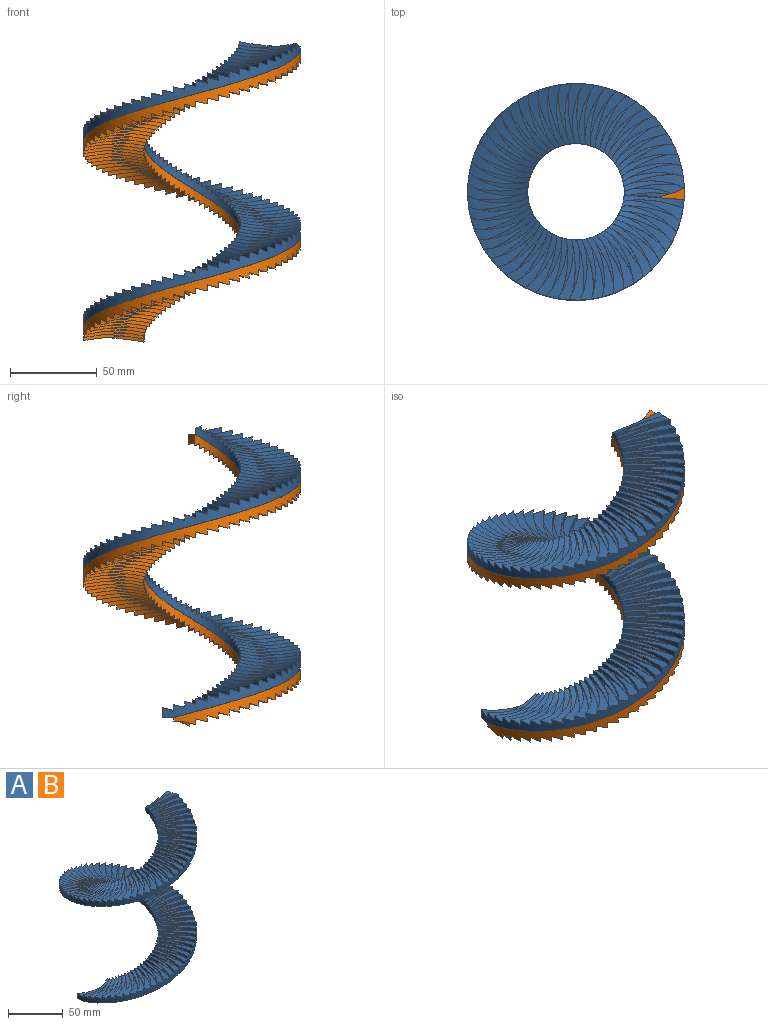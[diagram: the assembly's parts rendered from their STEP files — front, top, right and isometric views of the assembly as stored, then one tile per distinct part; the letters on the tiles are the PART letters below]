
ASSEMBLY  parts=2 mates=1
PART A: 370 faces, bbox 134.9x134.9x181.6 mm
  f0: plane 2.58x1.01mm, normal (0,0,-1), area 1mm2, adj f2,f184,f369
  f1: bspline ~40.21x16.63mm, area 94.5mm2, adj f2,f3,f4,f185,f368
  f2: cylinder r=27.93mm len=168.65mm, axis (0,0,-1), area 1520.9mm2, adj f0,f1,f4,f5,f6,f7,f8,f9
  f3: cylinder r=62.62mm len=167.8mm, axis (0,0,-1), area 3554.3mm2, adj f1,f185,f186,f187,f188,f189,f190,f191
  f4: bspline ~39.85x15.98mm, area 49.6mm2, adj f1,f2,f5,f185
  f5: bspline ~38.72x13.77mm, area 65.8mm2, adj f2,f4,f6,f185,f186
  f6: bspline ~37.98x15.95mm, area 41.2mm2, adj f2,f5,f7,f186,f187,f188
  f7: bspline ~39.79x14.14mm, area 55mm2, adj f2,f6,f8,f188
  f8: bspline ~37.93x15.94mm, area 41.3mm2, adj f2,f7,f9,f188,f189,f190
  f9: bspline ~40.42x16.75mm, area 66.7mm2, adj f2,f8,f10,f190
  f10: bspline ~37.46x15.96mm, area 41.2mm2, adj f2,f9,f11,f190,f191,f192
  f11: bspline ~40.61x19.84mm, area 66.8mm2, adj f2,f10,f12,f192
  f12: bspline ~36.57x15.97mm, area 41.2mm2, adj f2,f11,f13,f192,f193,f194
  f13: bspline ~40.36x23.15mm, area 54.7mm2, adj f2,f12,f14,f194
  f14: bspline ~35.31x15.95mm, area 41.2mm2, adj f2,f13,f15,f194,f195,f196
  f15: bspline ~39.67x26.21mm, area 66.4mm2, adj f2,f14,f16,f196
  f16: bspline ~33.65x17.74mm, area 41.3mm2, adj f2,f15,f17,f196,f197,f198
  f17: bspline ~38.53x28.98mm, area 66.8mm2, adj f2,f16,f18,f198
  f18: bspline ~31.59x21.16mm, area 41.2mm2, adj f2,f17,f19,f198,f199,f200
  f19: bspline ~36.98x31.43mm, area 66.5mm2, adj f2,f18,f20,f200
  f20: bspline ~29.21x24.34mm, area 41.2mm2, adj f2,f19,f21,f200,f201,f202
  f21: bspline ~35.03x33.54mm, area 54.8mm2, adj f2,f20,f22,f202
  f22: bspline ~27.26x26.55mm, area 41.2mm2, adj f2,f21,f23,f202,f203,f204
  f23: bspline ~35.28x32.68mm, area 66.5mm2, adj f2,f22,f24,f204
  f24: bspline ~29.88x23.55mm, area 41.3mm2, adj f2,f23,f25,f204,f205,f206
  f25: bspline ~36.63x29.97mm, area 66.9mm2, adj f2,f24,f26,f206
  f26: bspline ~32.17x20.27mm, area 41.2mm2, adj f2,f25,f27,f206,f207,f208
  f27: bspline ~37.58x26.95mm, area 54.9mm2, adj f2,f26,f28,f208
  f28: bspline ~34.11x16.81mm, area 41.2mm2, adj f2,f27,f29,f208,f209,f210
  f29: bspline ~38.12x23.63mm, area 54.9mm2, adj f2,f28,f30,f210
  f30: bspline ~35.67x15.94mm, area 41.3mm2, adj f2,f29,f31,f210,f211,f212
  f31: bspline ~38.25x20.05mm, area 66.6mm2, adj f2,f30,f32,f212
  f32: bspline ~36.84x15.95mm, area 41.3mm2, adj f2,f31,f33,f212,f213,f214
  f33: bspline ~37.95x16.63mm, area 67.1mm2, adj f2,f32,f34,f214
  f34: bspline ~37.61x15.98mm, area 41.2mm2, adj f2,f33,f35,f214,f215
  f35: bspline ~38.72x13.77mm, area 65.8mm2, adj f2,f34,f36,f215,f216
  f36: bspline ~37.98x15.95mm, area 41.2mm2, adj f2,f35,f37,f216,f217,f218
  f37: bspline ~39.79x14.14mm, area 55mm2, adj f2,f36,f38,f218
  f38: bspline ~37.93x15.94mm, area 41.3mm2, adj f2,f37,f39,f218,f219,f220
  f39: bspline ~40.42x16.75mm, area 66.7mm2, adj f2,f38,f40,f220
  f40: bspline ~37.46x15.96mm, area 41.2mm2, adj f2,f39,f41,f220,f221,f222
  f41: bspline ~40.61x19.84mm, area 66.8mm2, adj f2,f40,f42,f222
  f42: bspline ~36.57x15.97mm, area 41.2mm2, adj f2,f41,f43,f222,f223,f224
  f43: bspline ~40.36x23.15mm, area 54.7mm2, adj f2,f42,f44,f224
  f44: bspline ~35.31x15.95mm, area 41.2mm2, adj f2,f43,f45,f224,f225,f226
  f45: bspline ~39.67x26.21mm, area 66.4mm2, adj f2,f44,f46,f226
  f46: bspline ~33.65x17.74mm, area 41.3mm2, adj f2,f45,f47,f226,f227,f228
  f47: bspline ~38.53x28.98mm, area 66.8mm2, adj f2,f46,f48,f228
  f48: bspline ~31.59x21.16mm, area 41.2mm2, adj f2,f47,f49,f228,f229,f230
  f49: bspline ~36.98x31.43mm, area 66.5mm2, adj f2,f48,f50,f230
  f50: bspline ~29.21x24.35mm, area 41.2mm2, adj f2,f49,f51,f230,f231,f232
  f51: bspline ~35.03x33.54mm, area 54.8mm2, adj f2,f50,f52,f232
  f52: bspline ~27.26x26.55mm, area 41.2mm2, adj f2,f51,f53,f232,f233,f234
  f53: bspline ~35.28x32.68mm, area 66.5mm2, adj f2,f52,f54,f234
  f54: bspline ~29.88x23.55mm, area 41.3mm2, adj f2,f53,f55,f234,f235,f236
  f55: bspline ~36.63x29.97mm, area 66.9mm2, adj f2,f54,f56,f236
  f56: bspline ~32.17x20.27mm, area 41.2mm2, adj f2,f55,f57,f236,f237,f238
  f57: bspline ~37.58x26.95mm, area 54.9mm2, adj f2,f56,f58,f238
  f58: bspline ~34.11x16.81mm, area 41.2mm2, adj f2,f57,f59,f238,f239,f240
  f59: bspline ~38.12x23.63mm, area 54.9mm2, adj f2,f58,f60,f240
  f60: bspline ~35.67x15.94mm, area 41.3mm2, adj f2,f59,f61,f240,f241,f242
  f61: bspline ~38.25x20.05mm, area 66.6mm2, adj f2,f60,f62,f242
  f62: bspline ~36.84x15.95mm, area 41.3mm2, adj f2,f61,f63,f242,f243,f244
  f63: bspline ~37.95x16.63mm, area 67.1mm2, adj f2,f62,f64,f244
  f64: bspline ~37.61x15.98mm, area 41.2mm2, adj f2,f63,f65,f244,f245
  f65: bspline ~38.72x13.77mm, area 65.8mm2, adj f2,f64,f66,f245,f246
  f66: bspline ~37.98x15.95mm, area 41.2mm2, adj f2,f65,f67,f246,f247,f248
  f67: bspline ~39.79x14.14mm, area 55mm2, adj f2,f66,f68,f248
  f68: bspline ~37.93x15.94mm, area 41.3mm2, adj f2,f67,f69,f248,f249,f250
  f69: bspline ~40.42x16.75mm, area 66.7mm2, adj f2,f68,f70,f250
  f70: bspline ~37.46x15.96mm, area 41.2mm2, adj f2,f69,f71,f250,f251,f252
  f71: bspline ~40.61x19.84mm, area 66.8mm2, adj f2,f70,f72,f252
  f72: bspline ~36.57x15.97mm, area 41.2mm2, adj f2,f71,f73,f252,f253,f254
  f73: bspline ~40.36x23.15mm, area 54.7mm2, adj f2,f72,f74,f254
  f74: bspline ~35.31x15.95mm, area 41.2mm2, adj f2,f73,f75,f254,f255,f256
  f75: bspline ~39.67x26.21mm, area 66.4mm2, adj f2,f74,f76,f256
  f76: bspline ~33.65x17.74mm, area 41.3mm2, adj f2,f75,f77,f256,f257,f258
  f77: bspline ~38.53x28.98mm, area 66.8mm2, adj f2,f76,f78,f258
  f78: bspline ~31.59x21.16mm, area 41.2mm2, adj f2,f77,f79,f258,f259,f260
  f79: bspline ~36.98x31.43mm, area 66.5mm2, adj f2,f78,f80,f260
  f80: bspline ~29.21x24.34mm, area 41.2mm2, adj f2,f79,f81,f260,f261,f262
  f81: bspline ~35.03x33.54mm, area 54.8mm2, adj f2,f80,f82,f262
  f82: bspline ~27.26x26.55mm, area 41.2mm2, adj f2,f81,f83,f262,f263,f264
  f83: bspline ~35.28x32.68mm, area 66.5mm2, adj f2,f82,f84,f264
  f84: bspline ~29.88x23.55mm, area 41.3mm2, adj f2,f83,f85,f264,f265,f266
  f85: bspline ~36.63x29.97mm, area 66.9mm2, adj f2,f84,f86,f266
  f86: bspline ~32.17x20.27mm, area 41.2mm2, adj f2,f85,f87,f266,f267,f268
  f87: bspline ~37.58x26.95mm, area 54.9mm2, adj f2,f86,f88,f268
  f88: bspline ~34.11x16.81mm, area 41.2mm2, adj f2,f87,f89,f268,f269,f270
  f89: bspline ~38.12x23.63mm, area 54.9mm2, adj f2,f88,f90,f270
  f90: bspline ~35.67x15.94mm, area 41.3mm2, adj f2,f89,f91,f270,f271,f272
  f91: bspline ~38.25x20.05mm, area 66.6mm2, adj f2,f90,f92,f272
  f92: bspline ~36.84x15.95mm, area 41.3mm2, adj f2,f91,f93,f272,f273,f274
  f93: bspline ~37.95x16.63mm, area 67.1mm2, adj f2,f92,f94,f274
  f94: bspline ~37.61x15.98mm, area 41.2mm2, adj f2,f93,f95,f274,f275
  f95: bspline ~38.72x13.77mm, area 65.8mm2, adj f2,f94,f96,f275,f276
  f96: bspline ~37.98x15.95mm, area 41.2mm2, adj f2,f95,f97,f276,f277,f278
  f97: bspline ~39.79x14.14mm, area 55mm2, adj f2,f96,f98,f278
  f98: bspline ~37.93x15.94mm, area 41.3mm2, adj f2,f97,f99,f278,f279,f280
  f99: bspline ~40.42x16.75mm, area 66.7mm2, adj f2,f98,f100,f280
  f100: bspline ~37.46x15.96mm, area 41.2mm2, adj f2,f99,f101,f280,f281,f282
  f101: bspline ~40.61x19.84mm, area 66.8mm2, adj f2,f100,f102,f282
  f102: bspline ~36.57x15.97mm, area 41.2mm2, adj f2,f101,f103,f282,f283,f284
  f103: bspline ~40.36x23.15mm, area 54.7mm2, adj f2,f102,f104,f284
  f104: bspline ~35.31x15.95mm, area 41.2mm2, adj f2,f103,f105,f284,f285,f286
  f105: bspline ~39.67x26.21mm, area 66.4mm2, adj f2,f104,f106,f286
  f106: bspline ~33.65x17.74mm, area 41.3mm2, adj f2,f105,f107,f286,f287,f288
  f107: bspline ~38.53x28.98mm, area 66.8mm2, adj f2,f106,f108,f288
  f108: bspline ~31.59x21.16mm, area 41.2mm2, adj f2,f107,f109,f288,f289,f290
  f109: bspline ~36.98x31.43mm, area 66.5mm2, adj f2,f108,f110,f290
  f110: bspline ~29.21x24.35mm, area 41.2mm2, adj f2,f109,f111,f290,f291,f292
  f111: bspline ~35.03x33.54mm, area 54.8mm2, adj f2,f110,f112,f292
  f112: bspline ~27.26x26.55mm, area 41.2mm2, adj f2,f111,f113,f292,f293,f294
  f113: bspline ~35.28x32.68mm, area 66.5mm2, adj f2,f112,f114,f294
  f114: bspline ~29.88x23.55mm, area 41.3mm2, adj f2,f113,f115,f294,f295,f296
  f115: bspline ~36.63x29.97mm, area 66.9mm2, adj f2,f114,f116,f296
  f116: bspline ~32.17x20.27mm, area 41.2mm2, adj f2,f115,f117,f296,f297,f298
  f117: bspline ~37.58x26.95mm, area 54.9mm2, adj f2,f116,f118,f298
  f118: bspline ~34.11x16.81mm, area 41.2mm2, adj f2,f117,f119,f298,f299,f300
  f119: bspline ~38.12x23.63mm, area 54.9mm2, adj f2,f118,f120,f300
  f120: bspline ~35.67x15.94mm, area 41.3mm2, adj f2,f119,f121,f300,f301,f302
  f121: bspline ~38.25x20.05mm, area 66.6mm2, adj f2,f120,f122,f302
  f122: bspline ~36.84x15.95mm, area 41.3mm2, adj f2,f121,f123,f302,f303,f304
  f123: bspline ~37.95x16.63mm, area 67.1mm2, adj f2,f122,f124,f304
  f124: bspline ~37.61x15.98mm, area 41.2mm2, adj f2,f123,f125,f304,f305
  f125: bspline ~38.72x13.77mm, area 65.8mm2, adj f2,f124,f126,f305,f306
  f126: bspline ~37.98x15.95mm, area 41.2mm2, adj f2,f125,f127,f306,f307,f308
  f127: bspline ~39.79x14.14mm, area 55mm2, adj f2,f126,f128,f308
  f128: bspline ~37.93x15.94mm, area 41.3mm2, adj f2,f127,f129,f308,f309,f310
  f129: bspline ~40.42x16.75mm, area 66.7mm2, adj f2,f128,f130,f310
  f130: bspline ~37.46x15.96mm, area 41.2mm2, adj f2,f129,f131,f310,f311,f312
  f131: bspline ~40.61x19.84mm, area 66.8mm2, adj f2,f130,f132,f312
  f132: bspline ~36.57x15.97mm, area 41.2mm2, adj f2,f131,f133,f312,f313,f314
  f133: bspline ~40.36x23.15mm, area 54.7mm2, adj f2,f132,f134,f314
  f134: bspline ~35.31x15.95mm, area 41.2mm2, adj f2,f133,f135,f314,f315,f316
  f135: bspline ~39.67x26.21mm, area 66.4mm2, adj f2,f134,f136,f316
  f136: bspline ~33.65x17.74mm, area 41.3mm2, adj f2,f135,f137,f316,f317,f318
  f137: bspline ~38.53x28.98mm, area 66.8mm2, adj f2,f136,f138,f318
  f138: bspline ~31.59x21.16mm, area 41.2mm2, adj f2,f137,f139,f318,f319,f320
  f139: bspline ~36.98x31.43mm, area 66.5mm2, adj f2,f138,f140,f320
  f140: bspline ~29.21x24.34mm, area 41.2mm2, adj f2,f139,f141,f320,f321,f322
  f141: bspline ~35.03x33.54mm, area 54.8mm2, adj f2,f140,f142,f322
  f142: bspline ~27.26x26.55mm, area 41.2mm2, adj f2,f141,f143,f322,f323,f324
  f143: bspline ~35.28x32.68mm, area 66.5mm2, adj f2,f142,f144,f324
  f144: bspline ~29.88x23.55mm, area 41.3mm2, adj f2,f143,f145,f324,f325,f326
  f145: bspline ~36.63x29.97mm, area 66.9mm2, adj f2,f144,f146,f326
  f146: bspline ~32.17x20.27mm, area 41.2mm2, adj f2,f145,f147,f326,f327,f328
  f147: bspline ~37.58x26.95mm, area 54.9mm2, adj f2,f146,f148,f328
  f148: bspline ~34.11x16.81mm, area 41.2mm2, adj f2,f147,f149,f328,f329,f330
  f149: bspline ~38.12x23.63mm, area 54.9mm2, adj f2,f148,f150,f330
  f150: bspline ~35.67x15.94mm, area 41.3mm2, adj f2,f149,f151,f330,f331,f332
  f151: bspline ~38.25x20.05mm, area 66.6mm2, adj f2,f150,f152,f332
  f152: bspline ~36.84x15.95mm, area 41.3mm2, adj f2,f151,f153,f332,f333,f334
  f153: bspline ~37.95x16.63mm, area 67.1mm2, adj f2,f152,f154,f334
  f154: bspline ~37.61x15.98mm, area 41.2mm2, adj f2,f153,f155,f334,f335
  f155: bspline ~38.72x13.77mm, area 65.8mm2, adj f2,f154,f156,f335,f336
  f156: bspline ~37.98x15.95mm, area 41.2mm2, adj f2,f155,f157,f336,f337,f338
  f157: bspline ~39.79x14.14mm, area 55mm2, adj f2,f156,f158,f338
  f158: bspline ~37.93x15.94mm, area 41.3mm2, adj f2,f157,f159,f338,f339,f340
  f159: bspline ~40.42x16.75mm, area 66.7mm2, adj f2,f158,f160,f340
  f160: bspline ~37.46x15.96mm, area 41.2mm2, adj f2,f159,f161,f340,f341,f342
  f161: bspline ~40.61x19.84mm, area 66.8mm2, adj f2,f160,f162,f342
  f162: bspline ~36.57x15.97mm, area 41.2mm2, adj f2,f161,f163,f342,f343,f344
  f163: bspline ~40.36x23.15mm, area 54.7mm2, adj f2,f162,f164,f344
  f164: bspline ~35.31x15.95mm, area 41.2mm2, adj f2,f163,f165,f344,f345,f346
  f165: bspline ~39.67x26.21mm, area 66.4mm2, adj f2,f164,f166,f346
  f166: bspline ~33.65x17.74mm, area 41.3mm2, adj f2,f165,f167,f346,f347,f348
  f167: bspline ~38.53x28.98mm, area 66.8mm2, adj f2,f166,f168,f348
  f168: bspline ~31.59x21.16mm, area 41.2mm2, adj f2,f167,f169,f348,f349,f350
  f169: bspline ~36.98x31.43mm, area 66.5mm2, adj f2,f168,f170,f350
  f170: bspline ~29.21x24.35mm, area 41.2mm2, adj f2,f169,f171,f350,f351,f352
  f171: bspline ~35.03x33.54mm, area 54.8mm2, adj f2,f170,f172,f352
  f172: bspline ~27.26x26.55mm, area 41.2mm2, adj f2,f171,f173,f352,f353,f354
  f173: bspline ~35.28x32.68mm, area 66.5mm2, adj f2,f172,f174,f354
  f174: bspline ~29.88x23.55mm, area 41.3mm2, adj f2,f173,f175,f354,f355,f356
  f175: bspline ~36.63x29.97mm, area 66.9mm2, adj f2,f174,f176,f356
  f176: bspline ~32.17x20.27mm, area 41.2mm2, adj f2,f175,f177,f356,f357,f358
  f177: bspline ~37.58x26.95mm, area 54.9mm2, adj f2,f176,f178,f358
  f178: bspline ~34.11x16.81mm, area 41.2mm2, adj f2,f177,f179,f358,f359,f360
  f179: bspline ~38.12x23.63mm, area 54.9mm2, adj f2,f178,f180,f360
  f180: bspline ~35.67x15.94mm, area 41.3mm2, adj f2,f179,f181,f360,f361,f362
  f181: bspline ~38.25x20.05mm, area 66.6mm2, adj f2,f180,f182,f362
  f182: bspline ~36.84x15.95mm, area 41.3mm2, adj f2,f181,f183,f362,f363,f364
  f183: bspline ~37.95x16.63mm, area 67.1mm2, adj f2,f182,f184,f364
  f184: bspline ~37.61x15.98mm, area 51.8mm2, adj f0,f2,f183,f364,f365,f366,f369
  f185: bspline ~40.03x16.78mm, area 102.9mm2, adj f1,f3,f4,f5,f186
  f186: bspline ~39.98x15.05mm, area 56.2mm2, adj f3,f5,f6,f185,f187
  f187: bspline ~40.44x19.89mm, area 99.9mm2, adj f3,f6,f186,f188
  f188: bspline ~39.32x15.01mm, area 56.8mm2, adj f3,f6,f7,f8,f187,f189
  f189: bspline ~40.41x23.19mm, area 100mm2, adj f3,f8,f188,f190
  f190: bspline ~38.23x15mm, area 57.4mm2, adj f3,f8,f9,f10,f189,f191
  f191: bspline ~39.93x26.81mm, area 100mm2, adj f3,f10,f190,f192
  f192: bspline ~36.72x16.47mm, area 57.3mm2, adj f3,f10,f11,f12,f191,f193
  f193: bspline ~39.02x30.13mm, area 100.1mm2, adj f3,f12,f192,f194
  f194: bspline ~34.79x20.18mm, area 56.3mm2, adj f3,f12,f13,f14,f193,f195
  f195: bspline ~37.67x33.14mm, area 99.9mm2, adj f3,f14,f194,f196
  f196: bspline ~32.52x23.76mm, area 57mm2, adj f3,f14,f15,f16,f195,f197
  f197: bspline ~35.92x35.78mm, area 100mm2, adj f3,f16,f196,f198
  f198: bspline ~29.87x27.02mm, area 57.6mm2, adj f3,f16,f17,f18,f197,f199
  f199: bspline ~38.02x33.77mm, area 100.1mm2, adj f3,f18,f198,f200
  f200: bspline ~29.95x26.88mm, area 56.8mm2, adj f3,f18,f19,f20,f199,f201
  f201: bspline ~39.85x31.25mm, area 100mm2, adj f3,f20,f200,f202
  f202: bspline ~32.59x23.6mm, area 56.5mm2, adj f3,f20,f21,f22,f201,f203
  f203: bspline ~41.24x28.39mm, area 99.9mm2, adj f3,f22,f202,f204
  f204: bspline ~34.9x20.1mm, area 57.1mm2, adj f3,f22,f23,f24,f203,f205
  f205: bspline ~42.18x25.22mm, area 100mm2, adj f3,f24,f204,f206
  f206: bspline ~36.8x16.35mm, area 57.8mm2, adj f3,f24,f25,f26,f205,f207
  f207: bspline ~42.66x21.89mm, area 100.1mm2, adj f3,f26,f206,f208
  f208: bspline ~38.27x15.04mm, area 56.4mm2, adj f3,f26,f27,f28,f207,f209
  f209: bspline ~42.67x18.91mm, area 100mm2, adj f3,f28,f208,f210
  f210: bspline ~39.36x15.02mm, area 56.7mm2, adj f3,f28,f29,f30,f209,f211
  f211: bspline ~42.21x16.28mm, area 100mm2, adj f3,f30,f210,f212
  f212: bspline ~40.01x15mm, area 57.3mm2, adj f3,f30,f31,f32,f211,f213
  f213: bspline ~41.29x14.24mm, area 100mm2, adj f3,f32,f212,f214
  f214: bspline ~40.21x15.01mm, area 57.9mm2, adj f3,f32,f33,f34,f213,f215
  f215: bspline ~40.03x16.78mm, area 100.5mm2, adj f3,f34,f35,f214,f216
  f216: bspline ~39.98x15.05mm, area 56.2mm2, adj f3,f35,f36,f215,f217
  f217: bspline ~40.44x19.89mm, area 99.9mm2, adj f3,f36,f216,f218
  f218: bspline ~39.32x15.01mm, area 56.8mm2, adj f3,f36,f37,f38,f217,f219
  f219: bspline ~40.41x23.19mm, area 100mm2, adj f3,f38,f218,f220
  f220: bspline ~38.23x15mm, area 57.4mm2, adj f3,f38,f39,f40,f219,f221
  f221: bspline ~39.93x26.81mm, area 100mm2, adj f3,f40,f220,f222
  f222: bspline ~36.72x16.47mm, area 57.3mm2, adj f3,f40,f41,f42,f221,f223
  f223: bspline ~39.02x30.13mm, area 100.1mm2, adj f3,f42,f222,f224
  f224: bspline ~34.79x20.18mm, area 56.3mm2, adj f3,f42,f43,f44,f223,f225
  f225: bspline ~37.67x33.14mm, area 99.9mm2, adj f3,f44,f224,f226
  f226: bspline ~32.52x23.76mm, area 57mm2, adj f3,f44,f45,f46,f225,f227
  f227: bspline ~35.92x35.78mm, area 100mm2, adj f3,f46,f226,f228
  f228: bspline ~29.87x27.02mm, area 57.6mm2, adj f3,f46,f47,f48,f227,f229
  f229: bspline ~38.02x33.77mm, area 100.1mm2, adj f3,f48,f228,f230
  f230: bspline ~29.95x26.88mm, area 56.8mm2, adj f3,f48,f49,f50,f229,f231
  f231: bspline ~39.85x31.25mm, area 100mm2, adj f3,f50,f230,f232
  f232: bspline ~32.59x23.6mm, area 56.5mm2, adj f3,f50,f51,f52,f231,f233
  f233: bspline ~41.24x28.39mm, area 99.9mm2, adj f3,f52,f232,f234
  f234: bspline ~34.9x20.1mm, area 57.1mm2, adj f3,f52,f53,f54,f233,f235
  f235: bspline ~42.18x25.22mm, area 100mm2, adj f3,f54,f234,f236
  f236: bspline ~36.8x16.35mm, area 57.8mm2, adj f3,f54,f55,f56,f235,f237
  f237: bspline ~42.66x21.89mm, area 100.1mm2, adj f3,f56,f236,f238
  f238: bspline ~38.27x15.04mm, area 56.4mm2, adj f3,f56,f57,f58,f237,f239
  f239: bspline ~42.67x18.91mm, area 100mm2, adj f3,f58,f238,f240
  f240: bspline ~39.36x15.02mm, area 56.7mm2, adj f3,f58,f59,f60,f239,f241
  f241: bspline ~42.21x16.28mm, area 100mm2, adj f3,f60,f240,f242
  f242: bspline ~40.01x15mm, area 57.3mm2, adj f3,f60,f61,f62,f241,f243
  f243: bspline ~41.29x14.24mm, area 100mm2, adj f3,f62,f242,f244
  f244: bspline ~40.21x15.01mm, area 57.9mm2, adj f3,f62,f63,f64,f243,f245
  f245: bspline ~40.03x16.78mm, area 100.5mm2, adj f3,f64,f65,f244,f246
  f246: bspline ~39.98x15.05mm, area 56.2mm2, adj f3,f65,f66,f245,f247
  f247: bspline ~40.44x19.89mm, area 99.9mm2, adj f3,f66,f246,f248
  f248: bspline ~39.32x15.01mm, area 56.8mm2, adj f3,f66,f67,f68,f247,f249
  f249: bspline ~40.41x23.19mm, area 100mm2, adj f3,f68,f248,f250
  f250: bspline ~38.23x15mm, area 57.4mm2, adj f3,f68,f69,f70,f249,f251
  f251: bspline ~39.93x26.81mm, area 100mm2, adj f3,f70,f250,f252
  f252: bspline ~36.72x16.47mm, area 57.3mm2, adj f3,f70,f71,f72,f251,f253
  f253: bspline ~39.02x30.13mm, area 100.1mm2, adj f3,f72,f252,f254
  f254: bspline ~34.79x20.18mm, area 56.3mm2, adj f3,f72,f73,f74,f253,f255
  f255: bspline ~37.67x33.14mm, area 99.9mm2, adj f3,f74,f254,f256
  f256: bspline ~32.52x23.76mm, area 57mm2, adj f3,f74,f75,f76,f255,f257
  f257: bspline ~35.92x35.78mm, area 100mm2, adj f3,f76,f256,f258
  f258: bspline ~29.87x27.02mm, area 57.6mm2, adj f3,f76,f77,f78,f257,f259
  f259: bspline ~38.02x33.77mm, area 100.1mm2, adj f3,f78,f258,f260
  f260: bspline ~29.95x26.88mm, area 56.8mm2, adj f3,f78,f79,f80,f259,f261
  f261: bspline ~39.85x31.25mm, area 100mm2, adj f3,f80,f260,f262
  f262: bspline ~32.59x23.6mm, area 56.5mm2, adj f3,f80,f81,f82,f261,f263
  f263: bspline ~41.24x28.39mm, area 99.9mm2, adj f3,f82,f262,f264
  f264: bspline ~34.9x20.1mm, area 57.1mm2, adj f3,f82,f83,f84,f263,f265
  f265: bspline ~42.18x25.22mm, area 100mm2, adj f3,f84,f264,f266
  f266: bspline ~36.8x16.35mm, area 57.8mm2, adj f3,f84,f85,f86,f265,f267
  f267: bspline ~42.66x21.89mm, area 100.1mm2, adj f3,f86,f266,f268
  f268: bspline ~38.27x15.04mm, area 56.4mm2, adj f3,f86,f87,f88,f267,f269
  f269: bspline ~42.67x18.91mm, area 100mm2, adj f3,f88,f268,f270
  f270: bspline ~39.36x15.02mm, area 56.7mm2, adj f3,f88,f89,f90,f269,f271
  f271: bspline ~42.21x16.28mm, area 100mm2, adj f3,f90,f270,f272
  f272: bspline ~40.01x15mm, area 57.3mm2, adj f3,f90,f91,f92,f271,f273
  f273: bspline ~41.29x14.24mm, area 100mm2, adj f3,f92,f272,f274
  f274: bspline ~40.21x15.01mm, area 57.9mm2, adj f3,f92,f93,f94,f273,f275
  f275: bspline ~40.03x16.78mm, area 100.5mm2, adj f3,f94,f95,f274,f276
  f276: bspline ~39.98x15.05mm, area 56.2mm2, adj f3,f95,f96,f275,f277
  f277: bspline ~40.44x19.89mm, area 99.9mm2, adj f3,f96,f276,f278
  f278: bspline ~39.32x15.01mm, area 56.8mm2, adj f3,f96,f97,f98,f277,f279
  f279: bspline ~40.41x23.19mm, area 100mm2, adj f3,f98,f278,f280
  f280: bspline ~38.23x15mm, area 57.4mm2, adj f3,f98,f99,f100,f279,f281
  f281: bspline ~39.93x26.81mm, area 100mm2, adj f3,f100,f280,f282
  f282: bspline ~36.72x16.47mm, area 57.3mm2, adj f3,f100,f101,f102,f281,f283
  f283: bspline ~39.02x30.13mm, area 100.1mm2, adj f3,f102,f282,f284
  f284: bspline ~34.79x20.18mm, area 56.3mm2, adj f3,f102,f103,f104,f283,f285
  f285: bspline ~37.67x33.14mm, area 99.9mm2, adj f3,f104,f284,f286
  f286: bspline ~32.52x23.76mm, area 57mm2, adj f3,f104,f105,f106,f285,f287
  f287: bspline ~35.92x35.78mm, area 100mm2, adj f3,f106,f286,f288
  f288: bspline ~29.87x27.02mm, area 57.6mm2, adj f3,f106,f107,f108,f287,f289
  f289: bspline ~38.02x33.77mm, area 100.1mm2, adj f3,f108,f288,f290
  f290: bspline ~29.95x26.88mm, area 56.8mm2, adj f3,f108,f109,f110,f289,f291
  f291: bspline ~39.85x31.25mm, area 100mm2, adj f3,f110,f290,f292
  f292: bspline ~32.59x23.6mm, area 56.5mm2, adj f3,f110,f111,f112,f291,f293
  f293: bspline ~41.24x28.39mm, area 99.9mm2, adj f3,f112,f292,f294
  f294: bspline ~34.9x20.1mm, area 57.1mm2, adj f3,f112,f113,f114,f293,f295
  f295: bspline ~42.18x25.22mm, area 100mm2, adj f3,f114,f294,f296
  f296: bspline ~36.8x16.35mm, area 57.8mm2, adj f3,f114,f115,f116,f295,f297
  f297: bspline ~42.66x21.89mm, area 100.1mm2, adj f3,f116,f296,f298
  f298: bspline ~38.27x15.04mm, area 56.4mm2, adj f3,f116,f117,f118,f297,f299
  f299: bspline ~42.67x18.91mm, area 100mm2, adj f3,f118,f298,f300
  f300: bspline ~39.36x15.02mm, area 56.7mm2, adj f3,f118,f119,f120,f299,f301
  f301: bspline ~42.21x16.28mm, area 100mm2, adj f3,f120,f300,f302
  f302: bspline ~40.01x15mm, area 57.3mm2, adj f3,f120,f121,f122,f301,f303
  f303: bspline ~41.29x14.24mm, area 100mm2, adj f3,f122,f302,f304
  f304: bspline ~40.21x15.01mm, area 57.9mm2, adj f3,f122,f123,f124,f303,f305
  f305: bspline ~40.03x16.78mm, area 100.5mm2, adj f3,f124,f125,f304,f306
  f306: bspline ~39.98x15.05mm, area 56.2mm2, adj f3,f125,f126,f305,f307
  f307: bspline ~40.44x19.89mm, area 99.9mm2, adj f3,f126,f306,f308
  f308: bspline ~39.32x15.01mm, area 56.8mm2, adj f3,f126,f127,f128,f307,f309
  f309: bspline ~40.41x23.19mm, area 100mm2, adj f3,f128,f308,f310
  f310: bspline ~38.23x15mm, area 57.4mm2, adj f3,f128,f129,f130,f309,f311
  f311: bspline ~39.93x26.81mm, area 100mm2, adj f3,f130,f310,f312
  f312: bspline ~36.72x16.47mm, area 57.3mm2, adj f3,f130,f131,f132,f311,f313
  f313: bspline ~39.02x30.13mm, area 100.1mm2, adj f3,f132,f312,f314
  f314: bspline ~34.79x20.18mm, area 56.3mm2, adj f3,f132,f133,f134,f313,f315
  f315: bspline ~37.67x33.14mm, area 99.9mm2, adj f3,f134,f314,f316
  f316: bspline ~32.52x23.76mm, area 57mm2, adj f3,f134,f135,f136,f315,f317
  f317: bspline ~35.92x35.78mm, area 100mm2, adj f3,f136,f316,f318
  f318: bspline ~29.87x27.02mm, area 57.6mm2, adj f3,f136,f137,f138,f317,f319
  f319: bspline ~38.02x33.77mm, area 100.1mm2, adj f3,f138,f318,f320
  f320: bspline ~29.95x26.88mm, area 56.8mm2, adj f3,f138,f139,f140,f319,f321
  f321: bspline ~39.85x31.25mm, area 100mm2, adj f3,f140,f320,f322
  f322: bspline ~32.59x23.6mm, area 56.5mm2, adj f3,f140,f141,f142,f321,f323
  f323: bspline ~41.24x28.39mm, area 99.9mm2, adj f3,f142,f322,f324
  f324: bspline ~34.9x20.1mm, area 57.1mm2, adj f3,f142,f143,f144,f323,f325
  f325: bspline ~42.18x25.22mm, area 100mm2, adj f3,f144,f324,f326
  f326: bspline ~36.8x16.35mm, area 57.8mm2, adj f3,f144,f145,f146,f325,f327
  f327: bspline ~42.66x21.89mm, area 100.1mm2, adj f3,f146,f326,f328
  f328: bspline ~38.27x15.04mm, area 56.4mm2, adj f3,f146,f147,f148,f327,f329
  f329: bspline ~42.67x18.91mm, area 100mm2, adj f3,f148,f328,f330
  f330: bspline ~39.36x15.02mm, area 56.7mm2, adj f3,f148,f149,f150,f329,f331
  f331: bspline ~42.21x16.28mm, area 100mm2, adj f3,f150,f330,f332
  f332: bspline ~40.01x15mm, area 57.3mm2, adj f3,f150,f151,f152,f331,f333
  f333: bspline ~41.29x14.24mm, area 100mm2, adj f3,f152,f332,f334
  f334: bspline ~40.21x15.01mm, area 57.9mm2, adj f3,f152,f153,f154,f333,f335
  f335: bspline ~40.03x16.78mm, area 100.5mm2, adj f3,f154,f155,f334,f336
  f336: bspline ~39.98x15.05mm, area 56.2mm2, adj f3,f155,f156,f335,f337
  f337: bspline ~40.44x19.89mm, area 99.9mm2, adj f3,f156,f336,f338
  f338: bspline ~39.32x15.01mm, area 56.8mm2, adj f3,f156,f157,f158,f337,f339
  f339: bspline ~40.41x23.19mm, area 100mm2, adj f3,f158,f338,f340
  f340: bspline ~38.23x15mm, area 57.4mm2, adj f3,f158,f159,f160,f339,f341
  f341: bspline ~39.93x26.81mm, area 100mm2, adj f3,f160,f340,f342
  f342: bspline ~36.72x16.47mm, area 57.3mm2, adj f3,f160,f161,f162,f341,f343
  f343: bspline ~39.02x30.13mm, area 100.1mm2, adj f3,f162,f342,f344
  f344: bspline ~34.79x20.18mm, area 56.3mm2, adj f3,f162,f163,f164,f343,f345
  f345: bspline ~37.67x33.14mm, area 99.9mm2, adj f3,f164,f344,f346
  f346: bspline ~32.52x23.76mm, area 57mm2, adj f3,f164,f165,f166,f345,f347
  f347: bspline ~35.92x35.78mm, area 100mm2, adj f3,f166,f346,f348
  f348: bspline ~29.87x27.02mm, area 57.6mm2, adj f3,f166,f167,f168,f347,f349
  f349: bspline ~38.02x33.77mm, area 100.1mm2, adj f3,f168,f348,f350
  f350: bspline ~29.95x26.88mm, area 56.8mm2, adj f3,f168,f169,f170,f349,f351
  f351: bspline ~39.85x31.25mm, area 100mm2, adj f3,f170,f350,f352
  f352: bspline ~32.59x23.6mm, area 56.5mm2, adj f3,f170,f171,f172,f351,f353
  f353: bspline ~41.24x28.39mm, area 99.9mm2, adj f3,f172,f352,f354
  f354: bspline ~34.9x20.1mm, area 57.1mm2, adj f3,f172,f173,f174,f353,f355
  f355: bspline ~42.18x25.22mm, area 100mm2, adj f3,f174,f354,f356
  f356: bspline ~36.8x16.35mm, area 57.8mm2, adj f3,f174,f175,f176,f355,f357
  f357: bspline ~42.66x21.89mm, area 100.1mm2, adj f3,f176,f356,f358
  f358: bspline ~38.27x15.04mm, area 56.4mm2, adj f3,f176,f177,f178,f357,f359
  f359: bspline ~42.67x18.91mm, area 100mm2, adj f3,f178,f358,f360
  f360: bspline ~39.36x15.02mm, area 56.7mm2, adj f3,f178,f179,f180,f359,f361
  f361: bspline ~42.21x16.28mm, area 100mm2, adj f3,f180,f360,f362
  f362: bspline ~40.01x15mm, area 57.3mm2, adj f3,f180,f181,f182,f361,f363
  f363: bspline ~41.29x14.24mm, area 100mm2, adj f3,f182,f362,f364
  f364: bspline ~40.21x15.01mm, area 57.9mm2, adj f3,f182,f183,f184,f363,f365
  f365: bspline ~40.03x16.78mm, area 100.1mm2, adj f3,f184,f364,f366
  f366: bspline ~39.98x15.05mm, area 135.8mm2, adj f3,f184,f365,f367,f369
  f367: plane 18.92x7.22mm, normal (0,0,-1), area 49.3mm2, adj f3,f366,f369
  f368: plane 34.2x5.86mm, normal (-0.17,0.99,0), area 86.4mm2, adj f1,f2,f3,f369
  f369: bspline ~175.92x134.46mm, area 16036.2mm2, adj f0,f2,f3,f184,f366,f367,f368
PART B: same geometry as A
PLACE A rot(axis=(0,0,-1),13.9deg) t=(31.33,31.74,6.99)mm
PLACE B rot(axis=(0,1,0),180deg) t=(31.33,31.74,-86.77)mm
MATE cylindrical B.f3 <-> A.f3  axis (0,0,1) through (31.33,31.74,-41.91)mm
